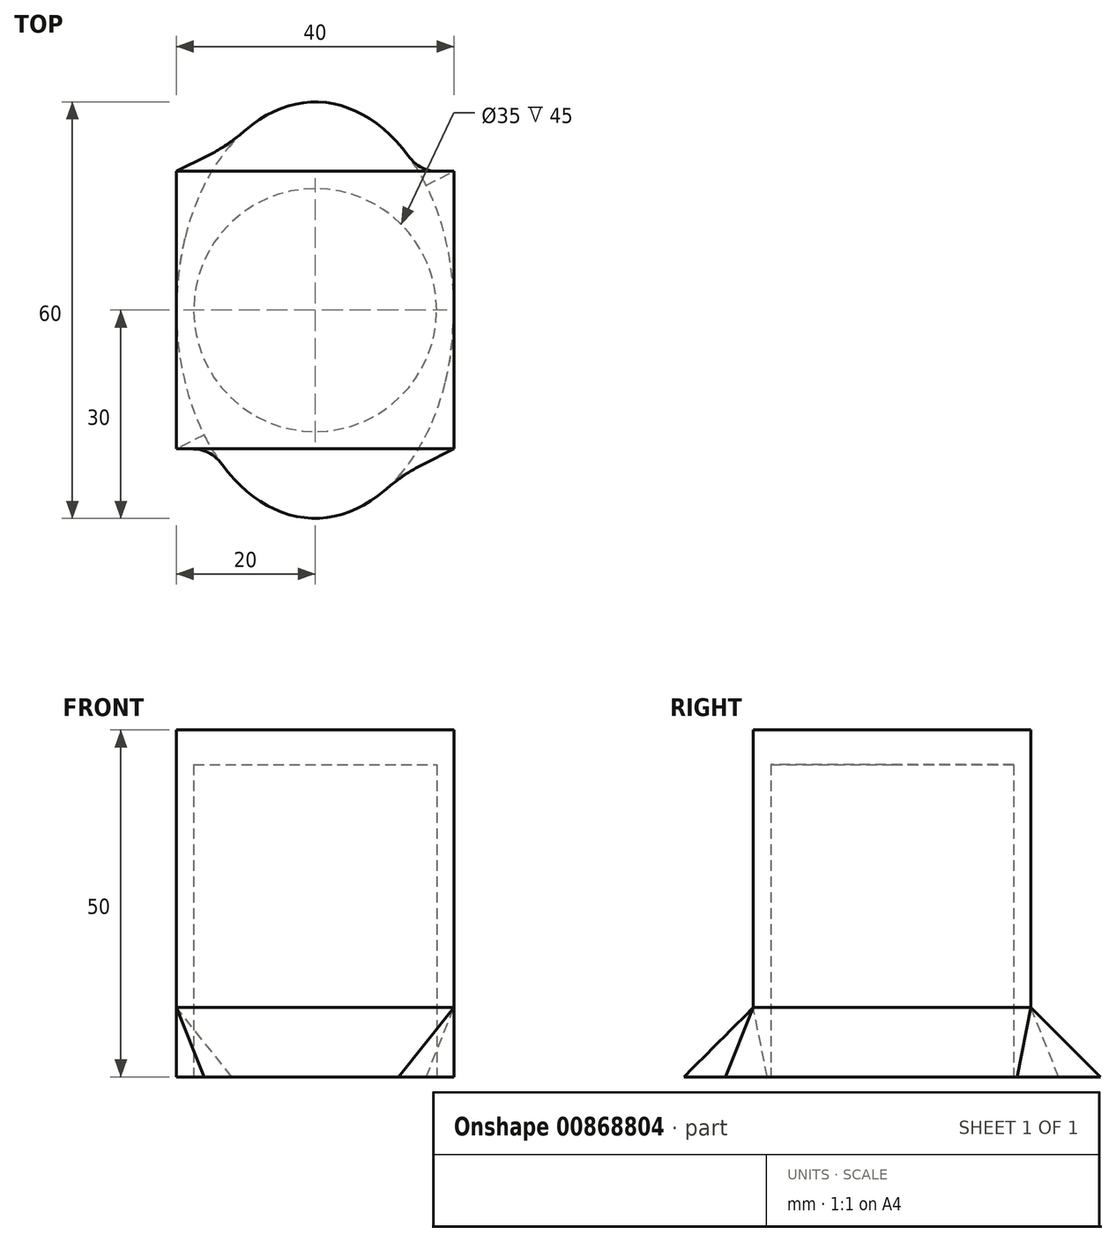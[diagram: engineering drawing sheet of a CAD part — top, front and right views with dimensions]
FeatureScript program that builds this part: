
annotation { "Feature Type Name" : "Feature", "Feature Type Description" : "" }
export const myFeature = defineFeature(function(context is Context, id is Id, definition is map)
    precondition{}
    {
        {
            var Q0;
            Q0=qCreatedBy(makeId("Top.planeOp"),FACE);
            var sketch = newSketch(context, id + "F0", { "sketchPlane" : qUnion([Q0])});
            skEllipse(sketch, "E0", {"center": v(0, 0) * mm, "majorRadius": 30 * mm, "minorRadius": 20 * mm, "majorAxis": v(0, 1)});
            skSolve(sketch);
        }
        {
            var Q0;
            Q0=qCreatedBy(makeId("Top.planeOp"),FACE);
            cPlane(context, id + "F1", {"entities" : qUnion([Q0]), "cplaneType" : CPlaneType.OFFSET, "offset" : 10 * mm, "width" : 150 * mm, "height" : 150 * mm});
        }
        {
            var Q0;
            Q0=qCreatedBy(id+"F1.planeOp",FACE);
            var sketch = newSketch(context, id + "F2", { "sketchPlane" : qUnion([Q0])});
            skLineSegment(sketch, "E1.bottom", {"start": v(20, 20) * mm, "end": v(-20, 20) * mm});
            skLineSegment(sketch, "E1.top", {"start": v(20, -20) * mm, "end": v(-20, -20) * mm});
            skLineSegment(sketch, "E1.left", {"start": v(20, 20) * mm, "end": v(20, -20) * mm});
            skLineSegment(sketch, "E1.right", {"start": v(-20, 20) * mm, "end": v(-20, -20) * mm});
            skPoint(sketch, "E1.middle", {"position": v(0, 0) * mm});
            skSolve(sketch);
        }
        {
            var Q0;
            Q0=makeQuery(id+"F0.imprint","IMPRINT",FACE,{"disambiguationData":[TD([[makeQuery(id+"F0.imprint","IMPRINT",EDGE,{"derivedFrom":sQuery(id+"F0.wireOp",EDGE,"E0")}),1.0]])]});
            var Q1;
            Q1=makeQuery(id+"F2.imprint","IMPRINT",FACE,{"disambiguationData":[TD([[makeQuery(id+"F2.imprint","IMPRINT",EDGE,{"derivedFrom":sQuery(id+"F2.wireOp",EDGE,"E1.bottom")}),1.0]])]});
            loft(context, id + "F3", {"sheetProfilesArray" : [{ "sheetProfileEntities" : qUnion([Q0]) }, { "sheetProfileEntities" : qUnion([Q1]) }]});
        }
        {
            var Q0;
            Q0=makeQuery(id+"F3.opLoft","CAP_FACE",FACE,{"disambiguationData":[OSD([makeQuery(id+"F2.imprint","IMPRINT",FACE,{"disambiguationData":[TD([[makeQuery(id+"F2.imprint","IMPRINT",EDGE,{"derivedFrom":sQuery(id+"F2.wireOp",EDGE,"E1.bottom")}),1.0]])]})])],"isStart":true});
            extrude(context, id + "F4", {"entities" : qUnion([Q0]), "operationType" : NewBodyOperationType.ADD, "depth" : 40 * mm, "offsetDistance" : 25 * mm});
        }
        {
            var Q0;
            Q0=makeQuery(id+"F3.opLoft","CAP_FACE",FACE,{"disambiguationData":[OSD([makeQuery(id+"F0.imprint","IMPRINT",FACE,{"disambiguationData":[TD([[makeQuery(id+"F0.imprint","IMPRINT",EDGE,{"derivedFrom":sQuery(id+"F0.wireOp",EDGE,"E0")}),1.0]])]})])],"isStart":true});
            var sketch = newSketch(context, id + "F5", { "sketchPlane" : qUnion([Q0])});
            skEllipse(sketch, "E2", {"center": v(0, 0) * mm, "majorRadius": 17.5 * mm, "minorRadius": 17.5 * mm, "majorAxis": v(0, 1)});
            skSolve(sketch);
        }
        {
            var Q0;
            Q0=makeQuery(id+"F5.imprint","IMPRINT",FACE,{"disambiguationData":[TD([[makeQuery(id+"F5.imprint","IMPRINT",EDGE,{"derivedFrom":sQuery(id+"F5.wireOp",EDGE,"E2")}),1.0]])]});
            extrude(context, id + "F6", {"entities" : qUnion([Q0]), "operationType" : NewBodyOperationType.REMOVE, "oppositeDirection" : true, "depth" : 45 * mm, "offsetDistance" : 25 * mm});
        }
    });
